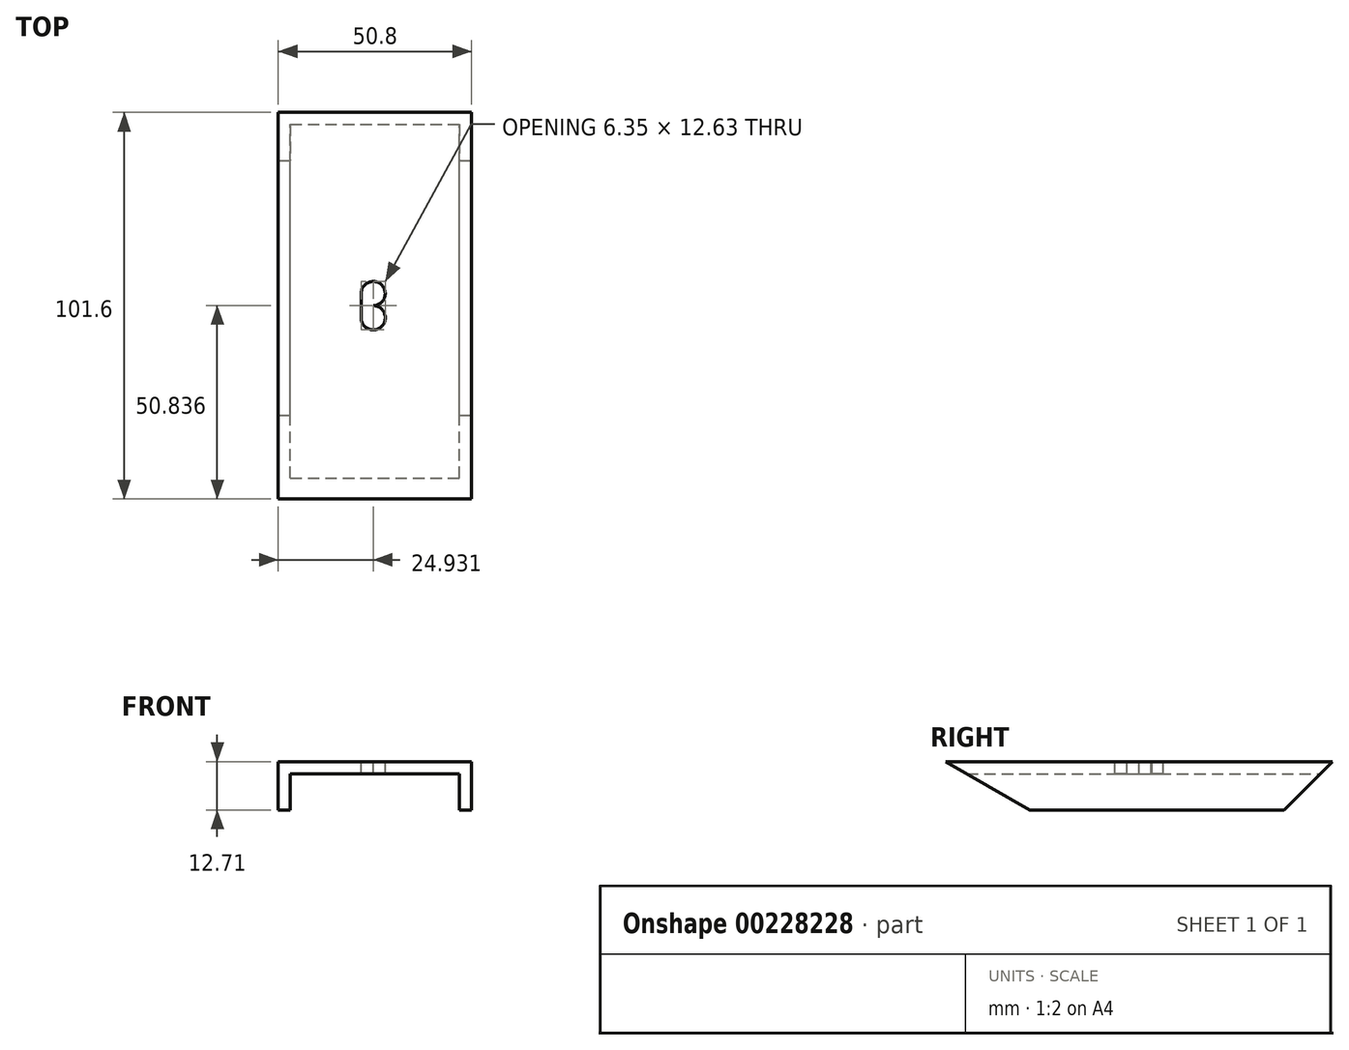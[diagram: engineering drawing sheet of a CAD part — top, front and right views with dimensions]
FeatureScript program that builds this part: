
annotation { "Feature Type Name" : "Feature", "Feature Type Description" : "" }
export const myFeature = defineFeature(function(context is Context, id is Id, definition is map)
    precondition{}
    {
        {
            var Q0;
            Q0=qCreatedBy(makeId("Top.planeOp"),FACE);
            var sketch = newSketch(context, id + "F0", { "sketchPlane" : qUnion([Q0])});
            skLineSegment(sketch, "E0.bottom", {"start": v(25.4, -50.8) * mm, "end": v(-25.4, -50.8) * mm});
            skLineSegment(sketch, "E0.top", {"start": v(25.4, 50.8) * mm, "end": v(-25.4, 50.8) * mm});
            skLineSegment(sketch, "E0.left", {"start": v(25.4, -50.8) * mm, "end": v(25.4, 50.8) * mm});
            skLineSegment(sketch, "E0.right", {"start": v(-25.4, -50.8) * mm, "end": v(-25.4, 50.8) * mm});
            skPoint(sketch, "E0.middle", {"position": v(0, 0) * mm});
            skSolve(sketch);
        }
        {
            var Q0;
            Q0=makeQuery(id+"F0.imprint","IMPRINT",FACE,{"disambiguationData":[TD([[makeQuery(id+"F0.imprint","IMPRINT",EDGE,{"derivedFrom":sQuery(id+"F0.wireOp",EDGE,"E0.bottom")}),-1.0]])]});
            extrude(context, id + "F1", {"entities" : qUnion([Q0]), "depth" : 3.17 * mm});
        }
        {
            var Q0;
            Q0=makeQuery(id+"F1.opExtrude","CAP_FACE",FACE,{"disambiguationData":[OSD([sQuery(id+"F0.wireOp",EDGE,"E0.bottom"),sQuery(id+"F0.wireOp",EDGE,"E0.top"),sQuery(id+"F0.wireOp",EDGE,"E0.left"),sQuery(id+"F0.wireOp",EDGE,"E0.right")])],"isStart":true});
            var sketch = newSketch(context, id + "F2", { "sketchPlane" : qUnion([Q0])});
            skLineSegment(sketch, "E1.bottom", {"start": v(25.4, 50.8) * mm, "end": v(22.22, 50.8) * mm});
            skLineSegment(sketch, "E1.top", {"start": v(25.4, -50.8) * mm, "end": v(22.23, -50.8) * mm});
            skLineSegment(sketch, "E1.left", {"start": v(25.4, 50.8) * mm, "end": v(25.4, -50.8) * mm});
            skLineSegment(sketch, "E1.right", {"start": v(22.22, 50.8) * mm, "end": v(22.23, -50.8) * mm});
            skLineSegment(sketch, "E2.bottom", {"start": v(-25.4, 50.8) * mm, "end": v(-22.23, 50.8) * mm});
            skLineSegment(sketch, "E2.top", {"start": v(-25.4, -50.8) * mm, "end": v(-22.22, -50.8) * mm});
            skLineSegment(sketch, "E2.left", {"start": v(-25.4, 50.8) * mm, "end": v(-25.4, -50.8) * mm});
            skLineSegment(sketch, "E2.right", {"start": v(-22.23, 50.8) * mm, "end": v(-22.22, -50.8) * mm});
            skSolve(sketch);
        }
        {
            var Q0;
            Q0=makeQuery(id+"F2.imprint","IMPRINT",FACE,{"disambiguationData":[TD([[makeQuery(id+"F2.imprint","IMPRINT",EDGE,{"derivedFrom":sQuery(id+"F2.wireOp",EDGE,"E2.bottom")}),1.0]])]});
            var Q1;
            Q1=makeQuery(id+"F2.imprint","IMPRINT",FACE,{"disambiguationData":[TD([[makeQuery(id+"F2.imprint","IMPRINT",EDGE,{"derivedFrom":sQuery(id+"F2.wireOp",EDGE,"E1.bottom")}),1.0]])]});
            extrude(context, id + "F3", {"entities" : qUnion([Q0, Q1]), "operationType" : NewBodyOperationType.ADD, "depth" : 9.52 * mm});
        }
        {
            var Q0;
            Q0=makeQuery(id+"F3.boolean.opBoolean","MERGE",FACE,{"derivedFrom":[makeQuery(id+"F1.opExtrude","SWEPT_FACE",FACE,{"disambiguationData":[OSD([sQuery(id+"F0.wireOp",EDGE,"E0.left")])]}),makeQuery(id+"F3.opExtrude","SWEPT_FACE",FACE,{"disambiguationData":[OSD([sQuery(id+"F2.wireOp",EDGE,"E1.left")])]})]});
            var sketch = newSketch(context, id + "F4", { "sketchPlane" : qUnion([Q0])});
            skLineSegment(sketch, "E3", {"start": v(-50.8, 3.18) * mm, "end": v(-28.8, -9.53) * mm});
            skLineSegment(sketch, "E4", {"start": v(50.8, 3.18) * mm, "end": v(38.1, -9.53) * mm});
            skSolve(sketch);
        }
        {
            var Q0;
            {var subQ0=sQuery(id+"F4.wireOp",EDGE,"E3");Q0=makeQuery(id+"F4.imprint","IMPRINT",FACE,{"disambiguationData":[TD([[makeQuery(id+"F4.imprint","IMPRINT",EDGE,{"derivedFrom":subQ0}),-1.0]])]});}
            var Q1;
            {var subQ0=sQuery(id+"F4.wireOp",EDGE,"E4");Q1=makeQuery(id+"F4.imprint","IMPRINT",FACE,{"disambiguationData":[TD([[makeQuery(id+"F4.imprint","IMPRINT",EDGE,{"derivedFrom":subQ0}),1.0]])]});}
            extrude(context, id + "F5", {"entities" : qUnion([Q0, Q1]), "operationType" : NewBodyOperationType.REMOVE, "oppositeDirection" : true, "depth" : 50.8 * mm});
        }
        {
            var Q0;
            Q0=makeQuery(id+"F1.opExtrude","CAP_FACE",FACE,{"disambiguationData":[OSD([sQuery(id+"F0.wireOp",EDGE,"E0.bottom"),sQuery(id+"F0.wireOp",EDGE,"E0.top"),sQuery(id+"F0.wireOp",EDGE,"E0.left"),sQuery(id+"F0.wireOp",EDGE,"E0.right")])],"isStart":false});
            var sketch = newSketch(context, id + "F6", { "sketchPlane" : qUnion([Q0])});
            skLineSegment(sketch, "E5", {"start": v(14.1, -6.35) * mm, "end": v(14.1, 6.35) * mm});
            skLineSegment(sketch, "E6", {"start": v(-15.04, 0) * mm, "end": v(-15.04, 6.35) * mm});
            skLineSegment(sketch, "E7", {"start": v(-15.04, 6.35) * mm, "end": v(14.1, 6.35) * mm});
            skLineSegment(sketch, "E8.MirrorCS", {"start": v(-15.04, -6.35) * mm, "end": v(14.1, -6.35) * mm});
            skLineSegment(sketch, "E9.MirrorCS", {"start": v(14.1, 6.35) * mm, "end": v(14.1, -6.35) * mm});
            skLineSegment(sketch, "E10.MirrorCS", {"start": v(-15.04, 0) * mm, "end": v(-15.04, -6.35) * mm});
            skLineSegment(sketch, "E11", {"start": v(-0.47, 6.35) * mm, "end": v(-0.47, 0) * mm});
            skPoint(sketch, "E11.endSnap0", {"position": v(-0.47, 6.35) * mm});
            skLineSegment(sketch, "E12", {"start": v(-0.47, -6.35) * mm, "end": v(-0.47, 0) * mm});
            skPoint(sketch, "E12.endSnap0", {"position": v(14.1, 0) * mm});
            skCircle(sketch, "E13", {"center": v(-0.47, 3.17) * mm, "radius": 3.18 * mm});
            skCircle(sketch, "E14", {"center": v(-0.47, -3.18) * mm, "radius": 3.18 * mm});
            skLineSegment(sketch, "E15", {"start": v(2.7, 3.27) * mm, "end": v(2.7, -3.27) * mm});
            skLineSegment(sketch, "E16", {"start": v(-3.64, -3.27) * mm, "end": v(-3.64, 3.38) * mm});
            skSolve(sketch);
        }
        {
            var Q0;
            {var subQ0=sQuery(id+"F6.wireOp",EDGE,"E11");Q0=makeQuery(id+"F6.imprint","IMPRINT",FACE,{"disambiguationData":[TD([[makeQuery(id+"F6.imprint","IMPRINT",EDGE,{"derivedFrom":subQ0}),-1.0]])]});}
            var Q1;
            {var subQ0=sQuery(id+"F6.wireOp",EDGE,"E11");Q1=makeQuery(id+"F6.imprint","IMPRINT",FACE,{"disambiguationData":[TD([[makeQuery(id+"F6.imprint","IMPRINT",EDGE,{"derivedFrom":subQ0}),1.0]])]});}
            var Q2;
            {var subQ0=sQuery(id+"F6.wireOp",EDGE,"E12");Q2=makeQuery(id+"F6.imprint","IMPRINT",FACE,{"disambiguationData":[TD([[makeQuery(id+"F6.imprint","IMPRINT",EDGE,{"derivedFrom":subQ0}),-1.0]])]});}
            var Q3;
            {var subQ0=sQuery(id+"F6.wireOp",EDGE,"E12");Q3=makeQuery(id+"F6.imprint","IMPRINT",FACE,{"disambiguationData":[TD([[makeQuery(id+"F6.imprint","IMPRINT",EDGE,{"derivedFrom":subQ0}),1.0]])]});}
            var Q4;
            {var subQ0=sQuery(id+"F6.wireOp",EDGE,"E15");var subQ1=sQuery(id+"F6.wireOp",EDGE,"E14");var subQ2=makeQuery(id+"F6.imprint","INTERSECT",VERTEX,{"disambiguationData":[OD(0.0)],"derivedFrom":[subQ1,subQ0]});Q4=makeQuery(id+"F6.imprint","IMPRINT",FACE,{"disambiguationData":[TD([[makeQuery(id+"F6.imprint","IMPRINT",EDGE,{"disambiguationData":[TD([[subQ2,-1.0]])],"derivedFrom":subQ1}),1.0]])]});}
            var Q5;
            {var subQ0=sQuery(id+"F6.wireOp",EDGE,"E16");var subQ1=sQuery(id+"F6.wireOp",EDGE,"E14");var subQ2=makeQuery(id+"F6.imprint","INTERSECT",VERTEX,{"disambiguationData":[OD(0.0)],"derivedFrom":[subQ1,subQ0]});Q5=makeQuery(id+"F6.imprint","IMPRINT",FACE,{"disambiguationData":[TD([[makeQuery(id+"F6.imprint","IMPRINT",EDGE,{"disambiguationData":[TD([[subQ2,1.0]])],"derivedFrom":subQ1}),1.0]])]});}
            var Q6;
            {var subQ1=sQuery(id+"F6.wireOp",EDGE,"E13");var subQ3=sQuery(id+"F6.wireOp",EDGE,"E15");var subQ4=makeQuery(id+"F6.imprint","INTERSECT",VERTEX,{"disambiguationData":[OD(1.0)],"derivedFrom":[subQ1,subQ3]});Q6=makeQuery(id+"F6.imprint","IMPRINT",FACE,{"disambiguationData":[TD([[makeQuery(id+"F6.imprint","IMPRINT",EDGE,{"disambiguationData":[TD([[subQ4,-1.0]])],"derivedFrom":subQ3}),-1.0]])]});}
            var Q7;
            {var subQ1=sQuery(id+"F6.wireOp",EDGE,"E13");var subQ3=sQuery(id+"F6.wireOp",EDGE,"E16");var subQ4=makeQuery(id+"F6.imprint","INTERSECT",VERTEX,{"disambiguationData":[OD(1.0)],"derivedFrom":[subQ1,subQ3]});Q7=makeQuery(id+"F6.imprint","IMPRINT",FACE,{"disambiguationData":[TD([[makeQuery(id+"F6.imprint","IMPRINT",EDGE,{"disambiguationData":[TD([[subQ4,1.0]])],"derivedFrom":subQ3}),-1.0]])]});}
            extrude(context, id + "F7", {"entities" : qUnion([Q0, Q1, Q2, Q3, Q4, Q5, Q6, Q7]), "operationType" : NewBodyOperationType.REMOVE, "oppositeDirection" : true, "depth" : 25.4 * mm});
        }
    });
